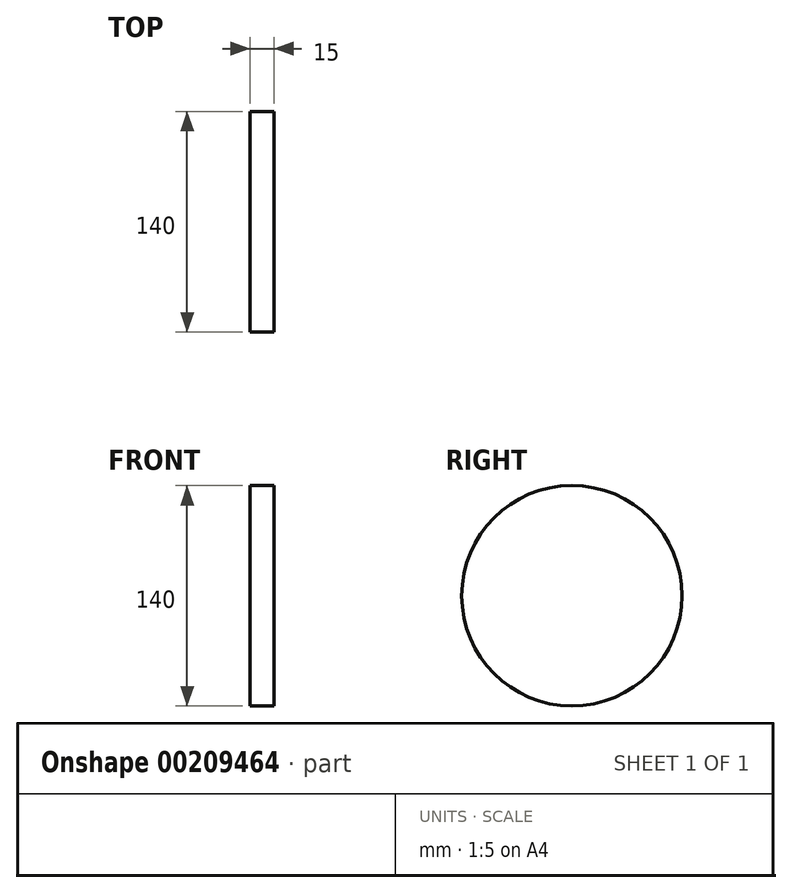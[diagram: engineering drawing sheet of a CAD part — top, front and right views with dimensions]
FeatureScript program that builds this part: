
annotation { "Feature Type Name" : "Feature", "Feature Type Description" : "" }
export const myFeature = defineFeature(function(context is Context, id is Id, definition is map)
    precondition{}
    {
        {
            var Q0;
            Q0=qCreatedBy(makeId("Right.planeOp"),FACE);
            var sketch = newSketch(context, id + "F0", { "sketchPlane" : qUnion([Q0])});
            skCircle(sketch, "E0", {"center": v(0, 0) * mm, "radius": 70 * mm});
            skSolve(sketch);
        }
        {
            var Q0;
            Q0=makeQuery(id+"F0.imprint","IMPRINT",FACE,{"disambiguationData":[TD([[makeQuery(id+"F0.imprint","IMPRINT",EDGE,{"derivedFrom":sQuery(id+"F0.wireOp",EDGE,"E0")}),1.0]])]});
            extrude(context, id + "F1", {"entities" : qUnion([Q0]), "depth" : 15 * mm});
        }
    });
